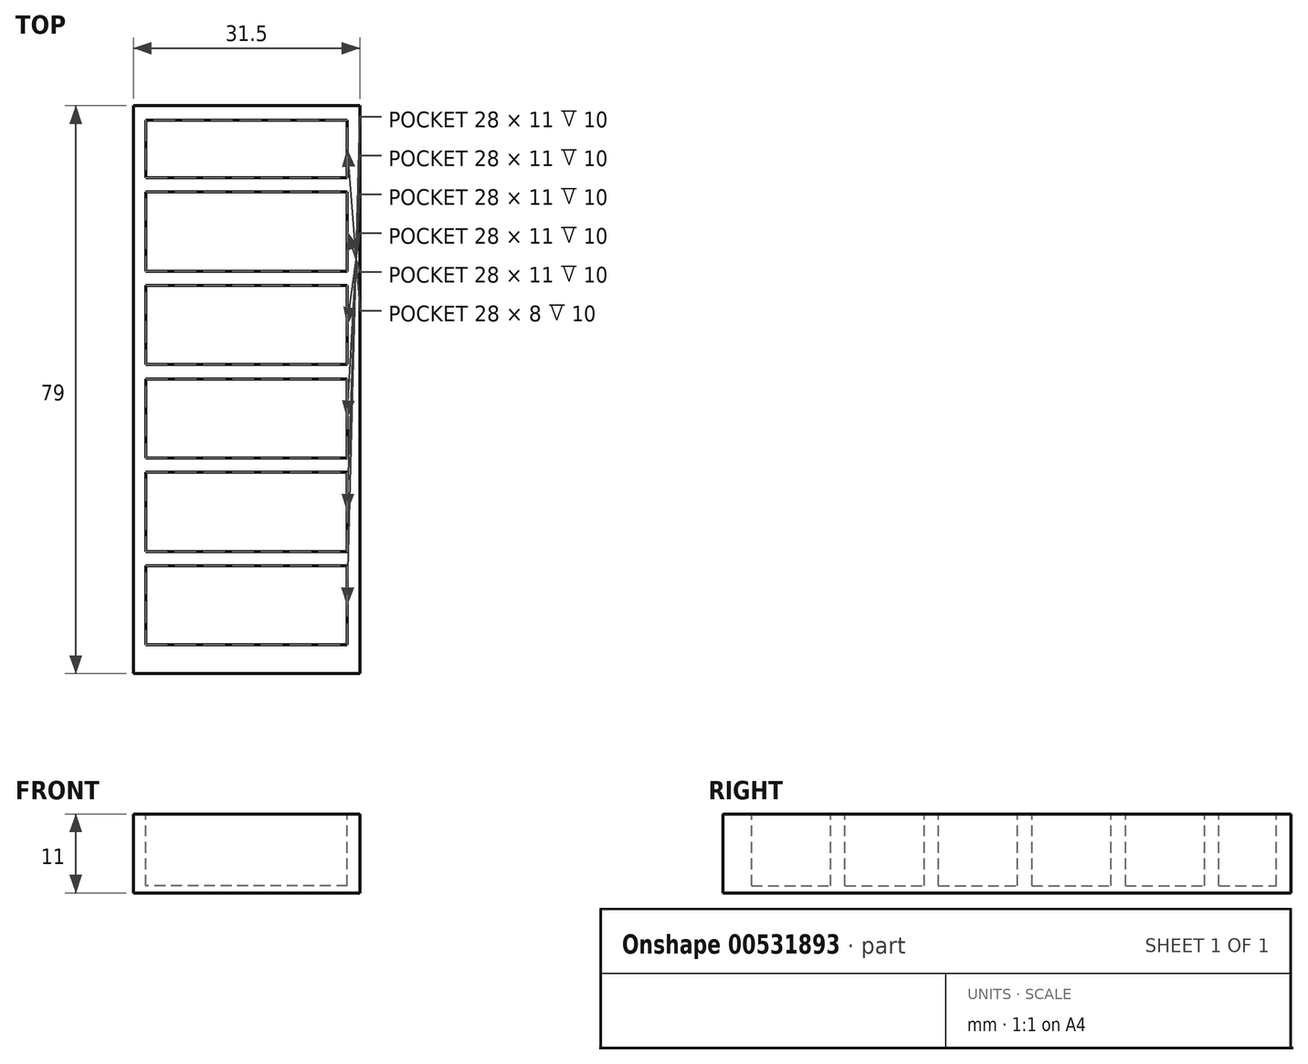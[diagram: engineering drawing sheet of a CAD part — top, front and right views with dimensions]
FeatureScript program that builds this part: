
annotation { "Feature Type Name" : "Feature", "Feature Type Description" : "" }
export const myFeature = defineFeature(function(context is Context, id is Id, definition is map)
    precondition{}
    {
        {
            var Q0;
            Q0=qCreatedBy(makeId("Front.planeOp"),FACE);
            var sketch = newSketch(context, id + "F0", { "sketchPlane" : qUnion([Q0])});
            skLineSegment(sketch, "E0.bottom", {"start": v(15.75, 5.5) * mm, "end": v(-15.75, 5.5) * mm});
            skLineSegment(sketch, "E0.top", {"start": v(15.75, -5.5) * mm, "end": v(-15.75, -5.5) * mm});
            skLineSegment(sketch, "E0.left", {"start": v(15.75, 5.5) * mm, "end": v(15.75, -5.5) * mm});
            skLineSegment(sketch, "E0.right", {"start": v(-15.75, 5.5) * mm, "end": v(-15.75, -5.5) * mm});
            skPoint(sketch, "E0.middle", {"position": v(0, 0) * mm});
            skSolve(sketch);
        }
        {
            var Q0;
            Q0 = qSketchRegion(id + "F0", true);
            extrude(context, id + "F1", {"entities" : qUnion([Q0]), "depth" : 79 * mm, "offsetDistance" : 25 * mm});
        }
        {
            var Q0;
            Q0=makeQuery(id+"F1.opExtrude","SWEPT_FACE",FACE,{"disambiguationData":[OSD([sQuery(id+"F0.wireOp",EDGE,"E0.bottom")])]});
            var sketch = newSketch(context, id + "F2", { "sketchPlane" : qUnion([Q0])});
            skLineSegment(sketch, "E1.bottom", {"start": v(14, -10) * mm, "end": v(-14, -10) * mm});
            skLineSegment(sketch, "E1.top", {"start": v(14, -2) * mm, "end": v(-14, -2) * mm});
            skLineSegment(sketch, "E1.left", {"start": v(14, -10) * mm, "end": v(14, -2) * mm});
            skLineSegment(sketch, "E1.right", {"start": v(-14, -10) * mm, "end": v(-14, -2) * mm});
            skPoint(sketch, "E1.middle", {"position": v(0, -6) * mm});
            skLineSegment(sketch, "E2.bottom", {"start": v(14, -23) * mm, "end": v(-14, -23) * mm});
            skLineSegment(sketch, "E2.top", {"start": v(14, -12) * mm, "end": v(-14, -12) * mm});
            skLineSegment(sketch, "E2.left", {"start": v(14, -23) * mm, "end": v(14, -12) * mm});
            skLineSegment(sketch, "E2.right", {"start": v(-14, -23) * mm, "end": v(-14, -12) * mm});
            skPoint(sketch, "E2.middle", {"position": v(0, -17.5) * mm});
            skLineSegment(sketch, "E3.bottom", {"start": v(14, -36) * mm, "end": v(-14, -36) * mm});
            skLineSegment(sketch, "E3.top", {"start": v(14, -25) * mm, "end": v(-14, -25) * mm});
            skLineSegment(sketch, "E3.left", {"start": v(14, -36) * mm, "end": v(14, -25) * mm});
            skLineSegment(sketch, "E3.right", {"start": v(-14, -36) * mm, "end": v(-14, -25) * mm});
            skPoint(sketch, "E3.middle", {"position": v(0, -30.5) * mm});
            skLineSegment(sketch, "E4.bottom", {"start": v(14, -49) * mm, "end": v(-14, -49) * mm});
            skLineSegment(sketch, "E4.top", {"start": v(14, -38) * mm, "end": v(-14, -38) * mm});
            skLineSegment(sketch, "E4.left", {"start": v(14, -49) * mm, "end": v(14, -38) * mm});
            skLineSegment(sketch, "E4.right", {"start": v(-14, -49) * mm, "end": v(-14, -38) * mm});
            skPoint(sketch, "E4.middle", {"position": v(0, -43.5) * mm});
            skLineSegment(sketch, "E5.bottom", {"start": v(14, -62) * mm, "end": v(-14, -62) * mm});
            skLineSegment(sketch, "E5.top", {"start": v(14, -51) * mm, "end": v(-14, -51) * mm});
            skLineSegment(sketch, "E5.left", {"start": v(14, -62) * mm, "end": v(14, -51) * mm});
            skLineSegment(sketch, "E5.right", {"start": v(-14, -62) * mm, "end": v(-14, -51) * mm});
            skPoint(sketch, "E5.middle", {"position": v(0, -56.5) * mm});
            skLineSegment(sketch, "E6.bottom", {"start": v(14, -75) * mm, "end": v(-14, -75) * mm});
            skLineSegment(sketch, "E6.top", {"start": v(14, -64) * mm, "end": v(-14, -64) * mm});
            skLineSegment(sketch, "E6.left", {"start": v(14, -75) * mm, "end": v(14, -64) * mm});
            skLineSegment(sketch, "E6.right", {"start": v(-14, -75) * mm, "end": v(-14, -64) * mm});
            skPoint(sketch, "E6.middle", {"position": v(0, -69.5) * mm});
            skSolve(sketch);
        }
        {
            var Q0;
            Q0 = qSketchRegion(id + "F2", true);
            extrude(context, id + "F3", {"entities" : qUnion([Q0]), "operationType" : NewBodyOperationType.REMOVE, "oppositeDirection" : true, "depth" : 10 * mm, "offsetDistance" : 25 * mm});
        }
    });
